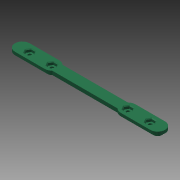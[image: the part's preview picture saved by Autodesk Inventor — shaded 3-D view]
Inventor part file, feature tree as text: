
AUTODESK INVENTOR PART (.ipt)
format: ipt  version: 2014 (Build 180170000, 170)  size: 246,784 bytes
history: native  units: in
note: dims shown in document units (in); Inventor stores cm internally (conversion verified against a paired STEP export)
features: extrude x6, sketch x6, plane x2, chamfer x2, mirror x1, projected_geometry x1
ambient origin geometry x8: Origin, YZ Plane, XZ Plane, XY Plane, X Axis, Y Axis, Z Axis, Center Point
bodies: Solid1 (feature_tree)
feature tree (18):
  extrude  "Extrusion1"  Depth=1.0in
  extrude  "Extrusion2"  Depth=0.1in
  extrude  "Extrusion3"  Depth=0.1in
  extrude  "Extrusion4"  Depth=0.75in
  extrude  "Extrusion5"  Depth=0.195in
  plane  "Work Plane2"
  extrude  "Extrusion6"  Depth=0.1in TaperAngle=0.0deg
  mirror  "Mirror1"
  chamfer  "Chamfer1"  Distance=0.23in
  chamfer  "Chamfer2"  Distance=0.0984in
  sketch  "Sketch1"  dims[d0=0.297in d1=1.0in]
  sketch  "Sketch2"  dims[d2=0.1in d3=0.0in d4=0.1in]
  sketch  "Sketch3"  dims[d5=0.1in d6=0.0in d7=0.12in]
  sketch  "Sketch4"  dims[d8=0.75in d9=0.25in]
  sketch  "Sketch5"  dims[d10=0.1in d11=0.0in d12=0.195in]
  sketch  "Sketch6"  dims[d13=0.0975in d14=0.1in d15=0.0in d16=0.23in d17=0.0984in d18=0.0in d19=1.05in d20=0.05in d21=0.0in d22=0.0in d25=0.025in d26=0.125in d27=45.0deg d28=0.025in d29=0.125in d30=45.0deg]
  projected_geometry  "Projected Loop1"
  plane  "Work Plane3"
